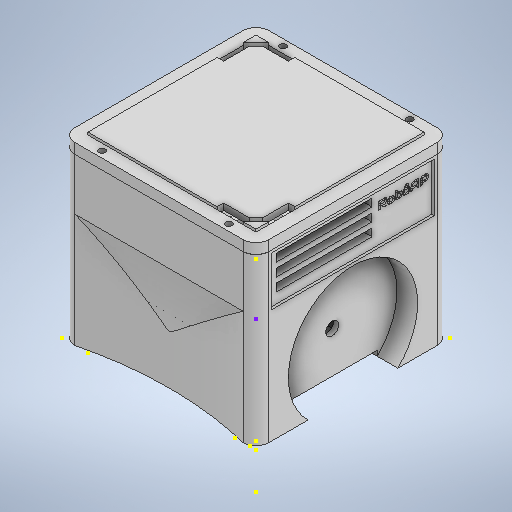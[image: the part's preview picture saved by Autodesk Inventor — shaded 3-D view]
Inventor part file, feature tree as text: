
AUTODESK INVENTOR PART (.ipt)
format: ipt  version: 2025.2 (Build 292293000, 293)  size: 1,842,688 bytes
history: native  units: mm
features: sketch x67, extrude x47, other x14, thread x13
ambient origin geometry x8: Origin, YZ Plane, XZ Plane, XY Plane, X Axis, Y Axis, Z Axis, Center Point
bodies: Body1 (feature_tree), Body2 (feature_tree), Body3 (feature_tree)
feature tree (141):
  other  "CaseInterno.ipt"
  other  "Tampa.ipt"
  other  "Sólido1"
  extrude  "Extrusão1"  Depth=75.0mm
  sketch  "Esboço2"  dims[d15=26.0mm d16=0.0mm d18=26.0mm d19=0.0mm]
  extrude  "Extrusão2"  Depth=5.0mm
  extrude  "Extrusão3"  Depth=15.0mm TaperAngle=0.0deg
  extrude  "Extrusão4"  Depth=15.0mm TaperAngle=0.0deg
  sketch  "Esboço3"  dims[d20=65.0mm d21=0.0mm d22=26.0mm d23=0.0mm]
  sketch  "Esboço4"  dims[d26=26.0mm d27=0.0mm d28=65.0mm d29=0.0mm]
  extrude  "Extrusão5"  Depth=26.0mm TaperAngle=0.0deg
  extrude  "Extrusão6"  Depth=26.0mm TaperAngle=0.0deg
  sketch  "Esboço7"  dims[d36=8.0mm d37=0.0mm d38=10.0mm d39=0.0mm]
  extrude  "Extrusão7"  Depth=26.0mm TaperAngle=0.0deg
  extrude  "Extrusão8"  Depth=65.0mm TaperAngle=0.0deg
  extrude  "Extrusão9"  Depth=8.0mm TaperAngle=0.0deg
  sketch  "Esboço13"  dims[d47=9.0mm d48=90.0deg]
  sketch  "Esboço14"  dims[d49=55.0mm d50=0.0mm d51=5.0mm]
  extrude  "Extrusão11"  Depth=5.0mm
  extrude  "Extrusão12"  Depth=10.0mm TaperAngle=0.0deg
  extrude  "Extrusão13"  Depth=6.0mm
  extrude  "Extrusão14"  TaperAngle=180.0deg  [1 undecoded]
  sketch  "Esboço16"  dims[d55=3.0mm d56=55.0mm]
  extrude  "Extrusão15"  TaperAngle=90.0deg  [1 undecoded]
  extrude  "Extrusão16"  Depth=5.0mm
  sketch  "Esboço17"  dims[d57=3.0mm d58=13.0mm d59=0.0mm]
  extrude  "Extrusão17"  Depth=13.0mm TaperAngle=0.0deg
  extrude  "Extrusão18"  Depth=55.0mm
  sketch  "Esboço20"  dims[d67=3.0mm d68=0.0mm d69=4.0mm]
  extrude  "Extrusão19"  Depth=13.0mm TaperAngle=0.0deg
  extrude  "Extrusão20"  Depth=24.0mm
  sketch  "Esboço23"  dims[d79=10.0mm d80=0.0mm d81=10.0mm d82=0.0mm]
  extrude  "Extrusão21"  Depth=3.0mm TaperAngle=0.0deg
  extrude  "Extrusão22"  Depth=4.0mm
  sketch  "Esboço26"  dims[d90=65.0mm d91=20.0mm d92=0.0mm]
  extrude  "Extrusão23"  Depth=4.0mm
  extrude  "Extrusão24"  Depth=3.0mm
  thread  "Rosca1"  [1 undecoded]
  thread  "Rosca2"  [1 undecoded]
  thread  "Rosca3"  [1 undecoded]
  thread  "Rosca4"  [1 undecoded]
  extrude  "Extrusão25"  Depth=10.0mm TaperAngle=0.0deg
  sketch  "Esboço30"  dims[d100=39.0mm d101=0.0mm d102=2.0mm d103=0.0mm]
  extrude  "Extrusão26"  Depth=10.0mm TaperAngle=0.0deg
  sketch  "Esboço32"  dims[d112=5.0mm d113=5.0mm d114=5.0mm d115=5.0mm d116=5.0mm d117=44.0mm d118=0.0mm]
  extrude  "Extrusão27"  Depth=65.0mm
  sketch  "Esboço34"  dims[d121=3.0mm d122=3.0mm]
  extrude  "Extrusão28"  Depth=20.0mm TaperAngle=0.0deg
  sketch  "Esboço36"  dims[d127=11.0mm d128=0.0mm d129=11.0mm d130=0.0mm d131=11.0mm d132=0.0mm]
  sketch  "Esboço37"  dims[d133=8.0mm d134=2.5mm]
  sketch  "Esboço38"  dims[d135=8.0mm d136=2.5mm]
  extrude  "Extrusão29"  Depth=36.0mm
  extrude  "Extrusão30"  TaperAngle=90.0deg  [1 undecoded]
  extrude  "Extrusão31"  Depth=19.0mm TaperAngle=0.0deg
  sketch  "Esboço41"  dims[d141=2.0mm d142=2.0mm]
  extrude  "Extrusão32"  Depth=2.0mm TaperAngle=0.0deg
  extrude  "Extrusão33"  Depth=63.0mm
  thread  "Rosca5"  [1 undecoded]
  thread  "Rosca6"  [1 undecoded]
  thread  "Rosca7"  [1 undecoded]
  thread  "Rosca8"  [1 undecoded]
  extrude  "Extrusão34"  Depth=5.0mm
  thread  "Rosca9"  [1 undecoded]
  thread  "Rosca10"  [1 undecoded]
  thread  "Rosca11"  [1 undecoded]
  thread  "Rosca12"  [1 undecoded]
  extrude  "Extrusão35"  Depth=3.0mm
  extrude  "Extrusão36"  Depth=3.0mm
  sketch  "Esboço47"  dims[d173=16.0mm]
  sketch  "Esboço48"  dims[d177=44.0mm d178=0.0mm]
  sketch  "Esboço49"  dims[d179=10.0mm d180=0.0mm]
  sketch  "Esboço50"  dims[d181=11.0mm d182=0.0mm]
  sketch  "Esboço51"  dims[d183=28.0mm d184=0.0mm]
  sketch  "Esboço52"  dims[d189=5.0mm d190=0.0mm]
  sketch  "Esboço53"  dims[d193=2.0mm d194=0.0mm]
  extrude  "Extrusão37"  Depth=11.0mm TaperAngle=0.0deg
  extrude  "Extrusão38"  Depth=11.0mm TaperAngle=0.0deg
  thread  "Rosca13"  [1 undecoded]
  extrude  "Extrusão39"  Depth=2.5mm
  sketch  "Esboço56"  dims[d199=22.0mm d200=0.0mm]
  sketch  "Esboço58"  dims[d201=2.0mm d202=0.0mm]
  extrude  "Extrusão40"  Depth=2.5mm
  extrude  "Extrusão42"  Depth=8.0mm
  extrude  "Extrusão43"  Depth=2.0mm
  sketch  "Esboço60"  dims[d227=1.9mm]
  sketch  "Esboço61"  dims[d228=1.9mm]
  extrude  "Extrusão44"  Depth=2.0mm
  extrude  "Extrusão45"  Depth=11.0mm TaperAngle=0.0deg
  extrude  "Extrusão46"  Depth=11.0mm TaperAngle=0.0deg
  sketch  "Esboço65"  dims[d231=14.0mm d232=0.0mm]
  extrude  "Extrusão47"  Depth=1.0mm
  sketch  "Esboço69"  dims[d246=22.25mm d247=8.0mm d248=10.0mm]
  extrude  "Extrusão48"  Depth=1.0mm TaperAngle=0.0deg
  extrude  "Extrusão49"  Depth=2.5mm
  other  "Edição direta16"
  other  "Edição direta17"
  sketch  "Esboço1"  dims[d0=75.0mm d1=75.0mm]
  sketch  "Esboço5"  dims[d30=5.0mm d31=8.0mm d32=0.0mm]
  sketch  "Esboço6"  dims[d33=10.0mm d34=0.0mm d35=5.0mm]
  sketch  "Esboço8"  dims[d40=2.0mm d44=6.0mm]
  sketch  "Esboço9"  dims[d45=6.0mm d46=180.0deg]
  sketch  "Esboço15"  dims[d52=5.0mm d53=13.0mm d54=0.0mm]
  sketch  "Esboço18"  dims[d60=41.0mm d61=0.0mm d62=24.0mm]
  sketch  "Esboço19"  dims[d63=13.0mm d64=0.0mm d65=3.0mm d66=0.0mm]
  sketch  "Esboço21"  dims[d70=4.0mm d71=4.0mm]
  sketch  "Esboço22"  dims[d72=90.0deg d73=3.0mm d74=3.0mm d75=3.0mm d76=3.0mm d77=10.0mm d78=0.0mm]
  sketch  "Esboço24"  dims[d83=10.0mm d84=0.0mm d85=10.0mm d86=0.0mm]
  sketch  "Esboço25"  dims[d87=13.0mm d88=0.0mm d89=65.0mm]
  sketch  "Esboço27"  dims[d93=9.5mm d94=36.0mm]
  sketch  "Esboço28"  dims[d95=59.0mm d96=90.0deg]
  sketch  "Esboço29"  dims[d97=36.0mm d98=19.0mm d99=0.0mm]
  sketch  "Esboço31"  dims[d104=1.0mm d105=63.0mm d106=1.0mm d107=0.0mm d108=0.0mm d109=0.0mm d110=5.0mm d111=90.0deg]
  sketch  "Esboço33"  dims[d119=3.0mm d120=3.0mm]
  sketch  "Esboço35"  dims[d123=10.0mm d124=0.0mm d125=11.0mm d126=0.0mm]
  sketch  "Esboço39"  dims[d137=2.5mm d138=8.0mm]
  sketch  "Esboço40"  dims[d139=2.0mm d140=2.0mm]
  sketch  "Esboço42"  dims[d143=10.0mm d144=0.0mm d145=11.0mm d146=0.0mm]
  sketch  "Esboço43"  dims[d147=11.0mm d148=0.0mm d149=11.0mm d150=0.0mm]
  sketch  "Esboço44"  dims[d151=11.0mm d152=0.0mm d153=1.0mm]
  sketch  "Esboço45"  dims[d154=1.0mm d155=0.0mm d156=1.0mm d157=0.0mm]
  sketch  "Esboço46"  dims[d171=2.5mm d172=2.5mm]
  sketch  "Esboço54"  dims[d195=22.0mm d196=0.0mm]
  sketch  "Esboço55"  dims[d197=2.0mm d198=0.0mm]
  sketch  "Esboço59"  dims[d211=2.0mm d212=0.0mm]
  sketch  "Esboço62"  dims[d229=4.0mm d230=0.0mm]
  sketch  "Esboço68"  dims[d245=10.0mm]
  sketch  "Esboço70"  dims[d249=-0.25mm d250=0.0mm d251=0.0mm]
  sketch  "Esboço71"  dims[d252=10.0mm d253=0.0mm d254=0.0mm d255=64.0mm d24=0.5mm d25=0.872665mm d158=0.5mm d159=0.872665mm d160=0.5mm d161=0.872665mm d174=0.5mm d175=0.872665mm d176=0.5mm]
  other  "Sólido1::CaseInterno.ipt"
  other  "OperaçãoIdentificador9"
  sketch  "Esboço26_1"  dims[d2=5.0mm d3=5.0mm]
  sketch  "Esboço32_1"  dims[d4=3.0mm d5=0.0mm d6=15.0mm d7=0.0mm]
  sketch  "Esboço42_1"  dims[d8=3.0mm d9=0.0mm d10=15.0mm d11=0.0mm]
  sketch  "Esboço43_1"  dims[d12=50.0mm d13=26.0mm d14=0.0mm]
  other  "Sólido1::Tampa.ipt"
  other  "OperaçãoIdentificador10"
  other  "Sólido1_1"
  other  "Mover14"
  other  "Mover15"
  other  "Sólido1_2"
  other  "Mover16"
note: 16 required parameter values undecoded (feature->parameter linkage not recoverable at this tier; creation-order binding heuristic only, values carry confidence <= 0.55)
